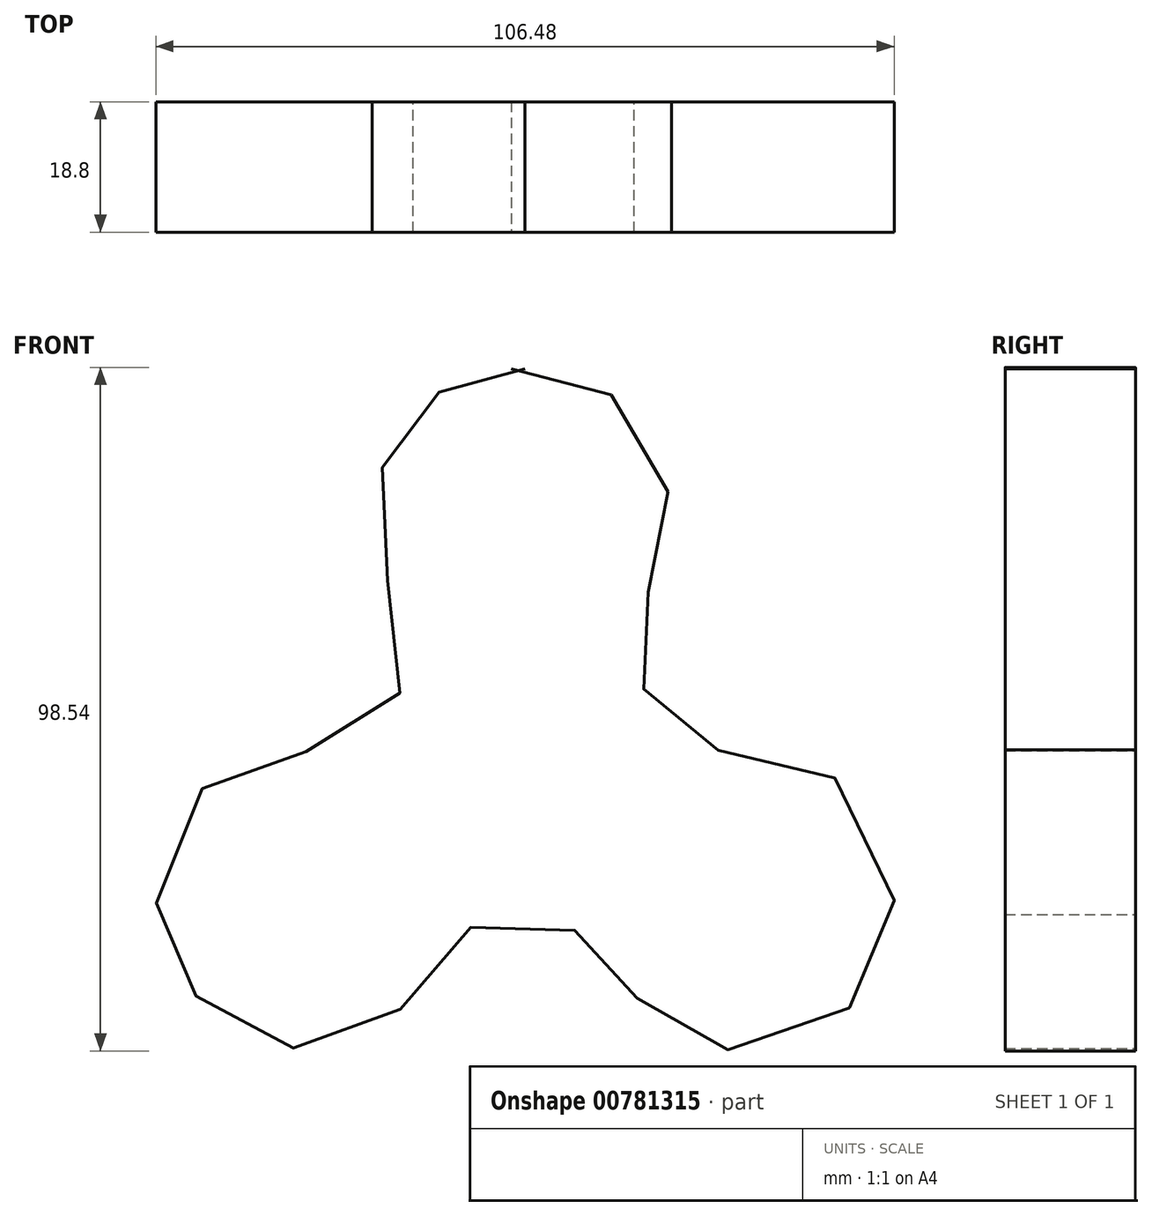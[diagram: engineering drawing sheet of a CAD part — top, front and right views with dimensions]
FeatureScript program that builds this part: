
annotation { "Feature Type Name" : "Feature", "Feature Type Description" : "" }
export const myFeature = defineFeature(function(context is Context, id is Id, definition is map)
    precondition{}
    {
        {
            var Q0;
            Q0=qCreatedBy(makeId("Front.planeOp"),FACE);
            var sketch = newSketch(context, id + "F0", { "sketchPlane" : qUnion([Q0])});
            skPoint(sketch, "E0.0.internal.snap0", {"position": v(1.98, 53.03) * mm});
            skPoint(sketch, "E0.18.internal.snap0", {"position": v(1.98, 53.03) * mm});
            skFitSpline(sketch, "E0", {"points": [v(0, 53.03) * mm, v(10.13, 51.53) * mm, v(16.54, 47.35) * mm, v(22.11, 37.32) * mm, v(22.4, 25.62) * mm, v(19.05, 19.5) * mm, v(17.93, 10.02) * mm, v(21, 4.17) * mm, v(27.94, -1.6) * mm, v(37, -2) * mm, v(50.8, -9.88) * mm, v(55.2, -24.85) * mm, v(51.58, -35.48) * mm, v(41.34, -44.15) * mm, v(26.76, -44.15) * mm, v(19.67, -39.42) * mm, v(14.55, -33.12) * mm, v(9.82, -28.4) * mm, v(1.98, -25.64) * mm, v(-8.3, -29.18) * mm, v(-13.82, -37.06) * mm, v(-23.67, -43.76) * mm, v(-33.91, -44.55) * mm, v(-43.76, -39.42) * mm, v(-48.5, -31.94) * mm, v(-51.23, -23.67) * mm, v(-47.7, -11.45) * mm, v(-37.46, -2.78) * mm, v(-28, -2) * mm, v(-18.55, 3.13) * mm, v(-14.22, 12.98) * mm, v(-18.94, 25.19) * mm, v(-19.38, 36.84) * mm, v(-16.03, 42.95) * mm, v(-11.09, 49.14) * mm, v(-2.97, 53.03) * mm, v(1.98, 53.03) * mm], "startDerivative": vector(385.53, -29.24) * mm, "endDerivative": vector(234.6, -27.27) * mm});
            skCircle(sketch, "E1", {"center": v(50.52, 32.14) * mm, "radius": 15.3 * mm});
            skSolve(sketch);
        }
        {
            var Q0;
            Q0=sQuery(id+"F0.wireOp",EDGE,"E0");
            extrude(context, id + "F1", {"bodyType" : ToolBodyType.SURFACE, "surfaceEntities" : qUnion([Q0]), "depth" : 18.8 * mm, "offsetDistance" : 25.4 * mm});
        }
    });
